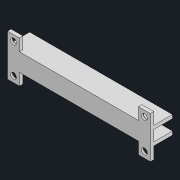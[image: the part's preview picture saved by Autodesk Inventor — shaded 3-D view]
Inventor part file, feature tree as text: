
AUTODESK INVENTOR PART (.ipt)
format: ipt  version: 2022.2 (Build 262287010, 287A)  size: 132,608 bytes
history: native  units: mm
features: extrude x3, sketch x3, mirror x2, chamfer x1
ambient origin geometry x8: Origin, YZ Plane, XZ Plane, XY Plane, X Axis, Y Axis, Z Axis, Center Point
bodies: Solid1 (feature_tree)
feature tree (9):
  extrude  "Extrusion1"  Depth=10.0mm TaperAngle=0.0deg
  extrude  "Extrusion2"  Depth=15.6mm
  extrude  "Extrusion4"  Depth=2.0mm TaperAngle=45.0deg
  chamfer  "Chamfer2"  [1 undecoded]
  mirror  "Mirror2"
  mirror  "Mirror3"
  sketch  "Sketch1"  dims[d3=120.0mm d4=0.0mm d9=10.0mm d10=0.0mm]
  sketch  "Sketch2"  dims[d18=9.0mm d19=15.6mm]
  sketch  "Sketch5"  dims[d21=0.0mm d22=0.0mm d24=2.0mm d25=45.0deg]
note: 1 required parameter value undecoded (feature->parameter linkage not recoverable at this tier; creation-order binding heuristic only, values carry confidence <= 0.55)
